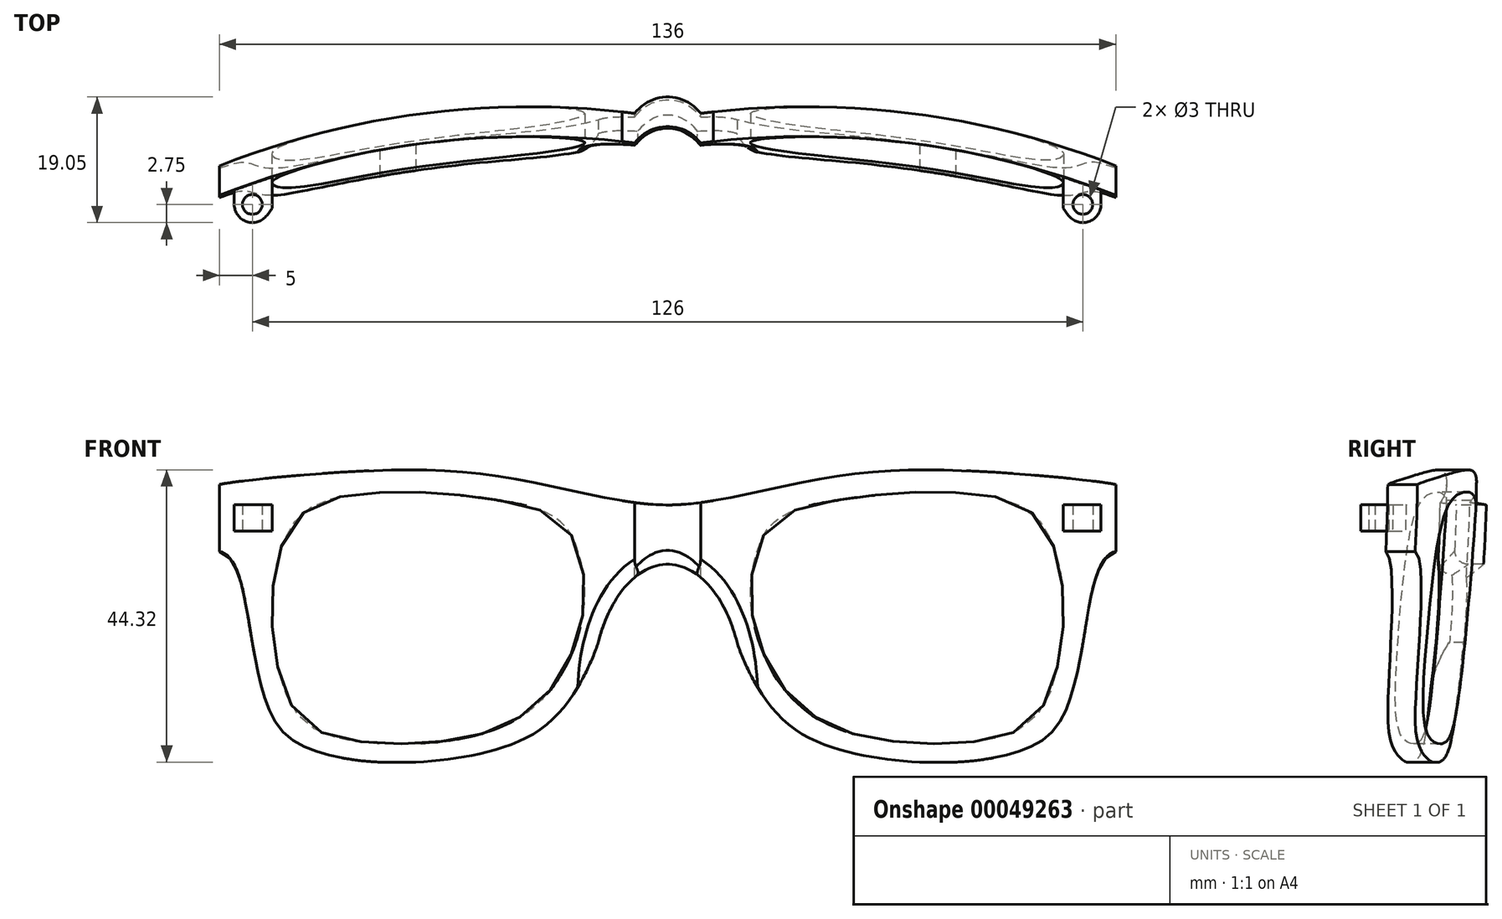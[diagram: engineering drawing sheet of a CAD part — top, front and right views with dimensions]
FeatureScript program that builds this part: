
annotation { "Feature Type Name" : "Feature", "Feature Type Description" : "" }
export const myFeature = defineFeature(function(context is Context, id is Id, definition is map)
    precondition{}
    {
        {
            var Q0;
            Q0=qCreatedBy(makeId("Top.planeOp"),FACE);
            var sketch = newSketch(context, id + "F0", { "sketchPlane" : qUnion([Q0])});
            skPoint(sketch, "E0", {"position": v(-5, 0) * mm});
            skPoint(sketch, "E1", {"position": v(-5, -2.5) * mm});
            skPoint(sketch, "E2", {"position": v(-31.5, 0) * mm});
            skPoint(sketch, "E3", {"position": v(-31.5, -2) * mm});
            skPoint(sketch, "E4", {"position": v(-68, 0) * mm});
            skPoint(sketch, "E5", {"position": v(-68, -10.5) * mm});
            skArc(sketch, "E6", {"start": v(-5, -2.5) * mm, "mid": v(-37, -2.58) * mm, "end": v(-68, -10.5) * mm});
            skArc(sketch, "E7.MirrorCS", {"start": v(5, -2.5) * mm, "mid": v(37, -2.58) * mm, "end": v(68, -10.5) * mm});
            skPoint(sketch, "E8", {"position": v(0, -6.25) * mm});
            skArc(sketch, "E9", {"start": v(-5, -2.5) * mm, "mid": v(0, 0) * mm, "end": v(5, -2.5) * mm});
            skSolve(sketch);
        }
        {
            var Q0;
            Q0=qCreatedBy(makeId("Right.planeOp"),FACE);
            var sketch = newSketch(context, id + "F1", { "sketchPlane" : qUnion([Q0])});
            skLineSegment(sketch, "E10", {"start": v(0, 0) * mm, "end": v(-4, 0) * mm});
            skPoint(sketch, "E11", {"position": v(4.2, 45) * mm});
            skPoint(sketch, "E12", {"position": v(0, 45) * mm});
            skLineSegment(sketch, "E13", {"start": v(4.2, 45) * mm, "end": v(0, 45) * mm});
            skFitSpline(sketch, "E14", {"points": [v(4.2, 45) * mm, v(3.05, 24.15) * mm, v(0, 0) * mm], "startDerivative": vector(-1.8, -42.59) * mm, "endDerivative": vector(-6.54, -47.35) * mm});
            skFitSpline(sketch, "E15", {"points": [v(0, 45) * mm, v(-0.95, 24.15) * mm, v(-4, 0) * mm], "startDerivative": vector(-1.05, -42.6) * mm, "endDerivative": vector(-6.87, -47.33) * mm});
            skSolve(sketch);
        }
        {
            var Q0;
            Q0=makeQuery(id+"F1.imprint","IMPRINT",FACE,{"disambiguationData":[TD([[makeQuery(id+"F1.imprint","IMPRINT",EDGE,{"derivedFrom":sQuery(id+"F1.wireOp",EDGE,"E10")}),-1.0]])]});
            var Q1;
            Q1=sQuery(id+"F0.wireOp",VERTEX,"E4");
            cPlane(context, id + "F2", {"entities" : qUnion([Q0, Q1]), "cplaneType" : CPlaneType.PLANE_POINT, "offset" : 200 * mm, "width" : 150 * mm, "height" : 150 * mm});
        }
        {
            var Q0;
            Q0=qCreatedBy(id+"F2.planeOp",FACE);
            var sketch = newSketch(context, id + "F3", { "sketchPlane" : qUnion([Q0])});
            skLineSegment(sketch, "E16", {"start": v(-9.17, 0) * mm, "end": v(-13.17, 0) * mm});
            skPoint(sketch, "E17", {"position": v(-9.17, 45) * mm});
            skLineSegment(sketch, "E18", {"start": v(-9.17, 45) * mm, "end": v(-4.67, 45) * mm});
            skArc(sketch, "E19", {"start": v(-9.17, 0) * mm, "mid": v(-5.8, 22.39) * mm, "end": v(-4.67, 45) * mm});
            skArc(sketch, "E20", {"start": v(-13.17, 0) * mm, "mid": v(-10.17, 22.41) * mm, "end": v(-9.17, 45) * mm});
            skSolve(sketch);
        }
        {
            var Q0;
            Q0 = qSketchRegion(id + "F3", true);
            var Q1;
            Q1 = qConstructionFilter(qBodyType(qCreatedBy(id + "F0" ,EDGE), BodyType.WIRE), ConstructionObject.NO);
            sweep(context, id + "F4", {"profiles" : qUnion([Q0]), "path" : qUnion([Q1]), "keepProfileOrientation" : true});
        }
        {
            var Q0;
            Q0=qCreatedBy(makeId("Front.planeOp"),FACE);
            var sketch = newSketch(context, id + "F5", { "sketchPlane" : qUnion([Q0])});
            skPoint(sketch, "E21", {"position": v(0, 30) * mm});
            skPoint(sketch, "E22", {"position": v(0, 10) * mm});
            skPoint(sketch, "E23", {"position": v(-10, 0) * mm});
            skFitSpline(sketch, "E24", {"points": [v(10.38, 18.76) * mm, v(15.05, 9.23) * mm, v(24.24, 2.49) * mm, v(43.67, 0) * mm, v(56.71, 3.23) * mm, v(60.64, 8.41) * mm, v(63.34, 20.03) * mm, v(67.24, 31.64) * mm, v(72.7, 31.71) * mm], "startDerivative": vector(13.07, -54.6) * mm, "endDerivative": vector(54.91, 0.07) * mm});
            skLineSegment(sketch, "E25", {"start": v(72.7, 31.71) * mm, "end": v(72.7, -9.78) * mm});
            skLineSegment(sketch, "E26", {"start": v(72.7, -9.78) * mm, "end": v(0, -11) * mm});
            skFitSpline(sketch, "E27.MirrorCS", {"points": [v(-10.38, 18.76) * mm, v(-15.05, 9.23) * mm, v(-24.24, 2.49) * mm, v(-43.67, 0) * mm, v(-56.71, 3.23) * mm, v(-60.64, 8.41) * mm, v(-63.34, 20.03) * mm, v(-67.24, 31.64) * mm, v(-72.7, 31.71) * mm], "startDerivative": vector(-13.07, -54.6) * mm, "endDerivative": vector(-54.91, 0.07) * mm});
            skLineSegment(sketch, "E28.MirrorCS", {"start": v(-72.7, -9.78) * mm, "end": v(0, -11) * mm});
            skLineSegment(sketch, "E29.MirrorCS", {"start": v(-72.7, 31.71) * mm, "end": v(-72.7, -9.78) * mm});
            skEllipse(sketch, "E30", {"center": v(0, 10) * mm, "majorRadius": 20 * mm, "minorRadius": 11.55 * mm, "majorAxis": v(0, 1)});
            skPoint(sketch, "E31", {"position": v(0, 39) * mm});
            skPoint(sketch, "E32", {"position": v(0, 45) * mm});
            skFitSpline(sketch, "E33", {"points": [v(6.92, 39.65) * mm, v(19.04, 42.12) * mm, v(33.07, 44.16) * mm, v(52.48, 43.77) * mm, v(68.38, 42.03) * mm, v(73.9, 41.02) * mm], "startDerivative": vector(9.45, 0) * mm, "endDerivative": vector(90.68, -9.64) * mm});
            skFitSpline(sketch, "E34.MirrorCS", {"points": [v(-6.92, 39.65) * mm, v(-19.04, 42.12) * mm, v(-33.07, 44.16) * mm, v(-52.48, 43.77) * mm, v(-68.38, 42.03) * mm, v(-73.9, 41.02) * mm], "startDerivative": vector(-9.45, 0) * mm, "endDerivative": vector(-90.68, -9.64) * mm});
            skFitSpline(sketch, "E35", {"points": [v(6.92, 39.65) * mm, v(0, 39) * mm, v(-6.92, 39.65) * mm], "startDerivative": vector(-12.15, -1.99) * mm, "endDerivative": vector(-12.15, 1.99) * mm});
            skLineSegment(sketch, "E36", {"start": v(73.9, 41.02) * mm, "end": v(73.9, 52.12) * mm});
            skLineSegment(sketch, "E37", {"start": v(73.9, 52.12) * mm, "end": v(-73.9, 52.12) * mm});
            skLineSegment(sketch, "E38", {"start": v(-73.9, 52.12) * mm, "end": v(-73.9, 41.02) * mm});
            skFitSpline(sketch, "E39", {"points": [v(19.34, 38.23) * mm, v(15.36, 35.56) * mm, v(13.14, 30.33) * mm, v(12.64, 23.86) * mm, v(16.17, 13.27) * mm, v(25.7, 5.16) * mm, v(44.04, 2.87) * mm, v(55.15, 6.22) * mm, v(59.38, 15.57) * mm, v(59.58, 28.94) * mm, v(54.53, 38.34) * mm, v(42.65, 40.92) * mm, v(32.85, 40.62) * mm, v(23.59, 39.34) * mm, v(19.34, 38.23) * mm]});
            skFitSpline(sketch, "E40.MirrorC", {"points": [v(-19.34, 38.23) * mm, v(-15.36, 35.56) * mm, v(-13.14, 30.33) * mm, v(-12.64, 23.86) * mm, v(-16.17, 13.27) * mm, v(-25.7, 5.16) * mm, v(-44.04, 2.87) * mm, v(-55.15, 6.22) * mm, v(-59.38, 15.57) * mm, v(-59.58, 28.94) * mm, v(-54.53, 38.34) * mm, v(-42.65, 40.92) * mm, v(-32.85, 40.62) * mm, v(-23.59, 39.34) * mm, v(-19.34, 38.23) * mm]});
            skPoint(sketch, "E41", {"position": v(-68.38, 32.03) * mm});
            skPoint(sketch, "E42", {"position": v(-68.38, 39.03) * mm});
            skPoint(sketch, "E43", {"position": v(-68.38, 35.03) * mm});
            skSolve(sketch);
        }
        {
            var Q0;
            Q0 = qSketchRegion(id + "F5", true);
            extrude(context, id + "F6", {"entities" : qUnion([Q0]), "operationType" : NewBodyOperationType.REMOVE, "oppositeDirection" : true, "depth" : 25 * mm, "hasSecondDirection" : true, "secondDirectionBound" : SecondDirectionBoundingType.THROUGH_ALL, "secondDirectionOppositeDirection" : false, "secondDirectionDepth" : 25 * mm});
        }
        {
            var Q0;
            Q0=qCreatedBy(makeId("Top.planeOp"),FACE);
            cPlane(context, id + "F7", {"entities" : qUnion([Q0]), "cplaneType" : CPlaneType.OFFSET, "offset" : 35.03 * mm, "width" : 150 * mm, "height" : 150 * mm});
        }
        {
            var Q0;
            Q0=qCreatedBy(id+"F7.planeOp",FACE);
            var sketch = newSketch(context, id + "F8", { "sketchPlane" : qUnion([Q0])});
            skPoint(sketch, "E44", {"position": v(-68, -6) * mm});
            skPoint(sketch, "E45", {"position": v(-67, -6) * mm});
            skPoint(sketch, "E46", {"position": v(-60, -6) * mm});
            skPoint(sketch, "E47", {"position": v(-64.5, -10.55) * mm});
            skPoint(sketch, "E48", {"position": v(-63, -10.55) * mm});
            skCircle(sketch, "E49", {"center": v(-63, -10.55) * mm, "radius": 1.5 * mm});
            skPoint(sketch, "E50", {"position": v(-65.75, -10.55) * mm});
            skArc(sketch, "E51", {"start": v(-65.75, -10.55) * mm, "mid": v(-63.86, -13.16) * mm, "end": v(-60.79, -12.18) * mm});
            skLineSegment(sketch, "E52", {"start": v(-60.79, -12.18) * mm, "end": v(-60, -11.11) * mm});
            skLineSegment(sketch, "E53", {"start": v(-60, -11.11) * mm, "end": v(-60, -6) * mm});
            skLineSegment(sketch, "E54", {"start": v(-65.75, -10.55) * mm, "end": v(-65.75, -6) * mm});
            skLineSegment(sketch, "E55", {"start": v(-65.75, -6) * mm, "end": v(-60, -6) * mm});
            skLineSegment(sketch, "E56.MirrorCS", {"start": v(60.79, -12.18) * mm, "end": v(60, -11.11) * mm});
            skArc(sketch, "E57.MirrorCS", {"start": v(65.75, -10.55) * mm, "mid": v(63.86, -13.16) * mm, "end": v(60.79, -12.18) * mm});
            skPoint(sketch, "E58.MirrorP", {"position": v(67, -6) * mm});
            skPoint(sketch, "E59.MirrorP", {"position": v(68, -6) * mm});
            skPoint(sketch, "E60.MirrorP", {"position": v(60, -6) * mm});
            skLineSegment(sketch, "E61.MirrorCS", {"start": v(65.75, -6) * mm, "end": v(60, -6) * mm});
            skLineSegment(sketch, "E62.MirrorCS", {"start": v(65.75, -10.55) * mm, "end": v(65.75, -6) * mm});
            skLineSegment(sketch, "E63.MirrorCS", {"start": v(60, -11.11) * mm, "end": v(60, -6) * mm});
            skPoint(sketch, "E64.MirrorP", {"position": v(64.5, -10.55) * mm});
            skCircle(sketch, "E65.MirrorC", {"center": v(63, -10.55) * mm, "radius": 1.5 * mm});
            skPoint(sketch, "E66.MirrorP", {"position": v(65.75, -10.55) * mm});
            skSolve(sketch);
        }
        {
            var Q0;
            Q0 = qSketchRegion(id + "F8", true);
            extrude(context, id + "F9", {"entities" : qUnion([Q0]), "operationType" : NewBodyOperationType.ADD, "depth" : 4 * mm});
        }
        {
            var Q0;
            Q0=makeQuery(id+"F6.boolean.opBoolean","INTERSECT",EDGE,{"derivedFrom":[makeQuery(id+"F4.opSweep","SWEPT_FACE",FACE,{"disambiguationData":[OSD([sQuery(id+"F0.wireOp",EDGE,"E6"),sQuery(id+"F3.wireOp",EDGE,"E20")])]}),makeQuery(id+"F6.opExtrude","SWEPT_FACE",FACE,{"disambiguationData":[OSD([sQuery(id+"F5.wireOp",EDGE,"E30")])]})]});
            var Q1;
            Q1=makeQuery(id+"F6.boolean.opBoolean","INTERSECT",EDGE,{"derivedFrom":[makeQuery(id+"F4.opSweep","SWEPT_FACE",FACE,{"disambiguationData":[OSD([sQuery(id+"F0.wireOp",EDGE,"E9"),sQuery(id+"F3.wireOp",EDGE,"E20")])]}),makeQuery(id+"F6.opExtrude","SWEPT_FACE",FACE,{"disambiguationData":[OSD([sQuery(id+"F5.wireOp",EDGE,"E30")])]})]});
            var Q2;
            Q2=makeQuery(id+"F6.boolean.opBoolean","INTERSECT",EDGE,{"derivedFrom":[makeQuery(id+"F4.opSweep","SWEPT_FACE",FACE,{"disambiguationData":[OSD([sQuery(id+"F0.wireOp",EDGE,"E7.MirrorCS"),sQuery(id+"F3.wireOp",EDGE,"E20")])]}),makeQuery(id+"F6.opExtrude","SWEPT_FACE",FACE,{"disambiguationData":[OSD([sQuery(id+"F5.wireOp",EDGE,"E30")])]})]});
            fillet(context, id + "F10", {"entities" : qUnion([Q0, Q1, Q2]), "radius" : 2 * mm, "tangentPropagation" : true, "allowEdgeOverflow" : false});
        }
    });
